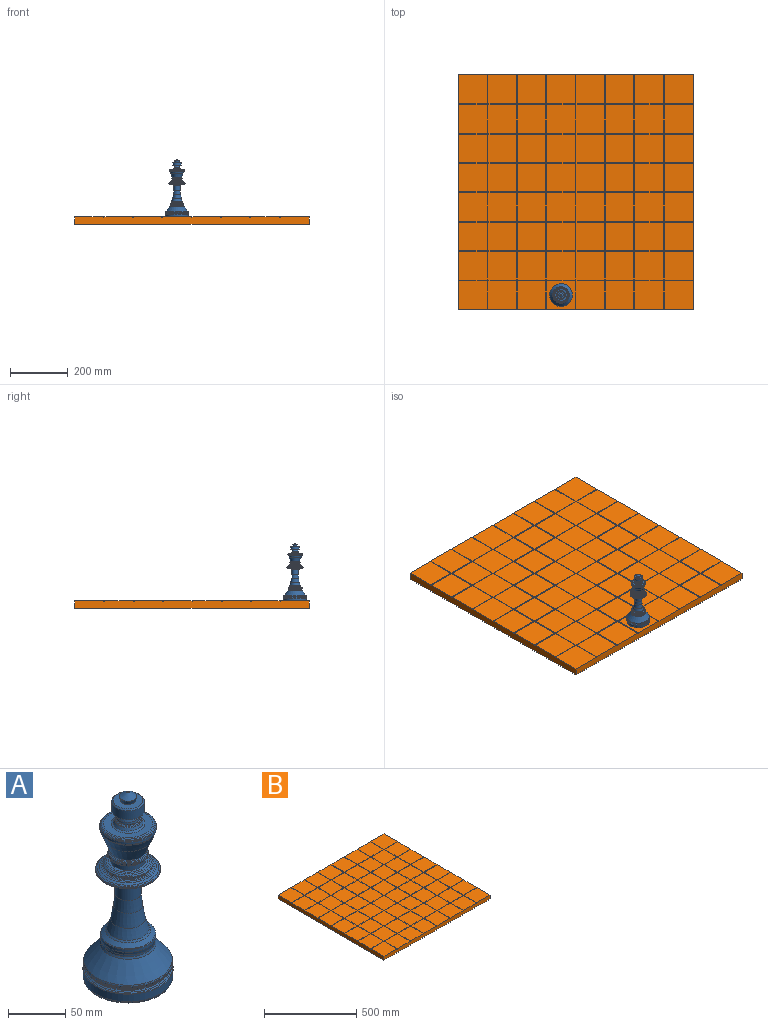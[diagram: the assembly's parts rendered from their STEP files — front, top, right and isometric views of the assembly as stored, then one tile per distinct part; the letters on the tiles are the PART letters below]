
ASSEMBLY  parts=2 mates=1
PART A: 79 faces, bbox 78.8x78.8x198.1 mm
  f0: cone r=0.97mm half-angle=57.7deg, axis (0,0,-1), area 220.6mm2, adj f1,f76
  f1: plane 1.95x1.95mm, normal (0,0,1), area 3mm2, adj f0
  f2: plane 77.2x77.2mm, normal (0,0,-1), area 4681mm2, adj f3
  f3: cone r=39.06mm half-angle=15.9deg, axis (0,0,1), area 409.4mm2, adj f2,f4
  f4: cone r=39.41mm half-angle=2.4deg, axis (0,0,1), area 2062.8mm2, adj f3,f5
  f5: cone r=39.06mm half-angle=38.7deg, axis (0,0,-1), area 138.9mm2, adj f4,f6
  f6: cone r=38mm half-angle=53.7deg, axis (0,0,-1), area 319.8mm2, adj f5,f7
  f7: cone r=36.85mm half-angle=47.9deg, axis (0,0,-1), area 362mm2, adj f6,f8
  f8: cone r=36.53mm half-angle=22.2deg, axis (0,0,-1), area 195.2mm2, adj f7,f9
  f9: cone r=37.16mm half-angle=30.8deg, axis (0,0,1), area 285.3mm2, adj f8,f10
  f10: cone r=38.07mm half-angle=39.3deg, axis (0,0,1), area 338.8mm2, adj f9,f11
  f11: cone r=38.75mm half-angle=27deg, axis (0,0,1), area 362mm2, adj f10,f12
  f12: cone r=39.06mm half-angle=13.8deg, axis (0,0,1), area 315.7mm2, adj f11,f13
  f13: cone r=38.56mm half-angle=22.2deg, axis (0,0,-1), area 322.8mm2, adj f12,f14
  f14: cone r=24.39mm half-angle=38.7deg, axis (0,0,-1), area 4485.2mm2, adj f13,f15
  f15: cone r=23.55mm half-angle=22.2deg, axis (0,0,-1), area 337.6mm2, adj f14,f16
  f16: cylinder r=23.55mm len=47.1mm, axis (0,0,1), area 298.9mm2, adj f15,f17
  f17: cone r=24.1mm half-angle=10.2deg, axis (0,0,1), area 468.6mm2, adj f16,f18
  f18: cylinder r=24.1mm len=48.2mm, axis (0,0,1), area 484.1mm2, adj f17,f19
  f19: cone r=23.65mm half-angle=38.7deg, axis (0,0,-1), area 108.7mm2, adj f18,f20
  f20: cone r=19.7mm half-angle=49.8deg, axis (0,0,-1), area 704.5mm2, adj f19,f21
  f21: cone r=18.38mm half-angle=38.7deg, axis (0,0,-1), area 253mm2, adj f20,f22
  f22: cone r=15.18mm half-angle=17deg, axis (0,0,-1), area 1156.2mm2, adj f21,f23
  f23: cone r=12.68mm half-angle=9.8deg, axis (0,0,-1), area 1278.9mm2, adj f22,f24
  f24: cone r=11.45mm half-angle=5.6deg, axis (0,0,-1), area 967.8mm2, adj f23,f25
  f25: cylinder r=11.45mm len=22.89mm, axis (0,0,1), area 1421.3mm2, adj f24,f26
  f26: plane 23.55x23.55mm, normal (0,0,-1), area 23.9mm2, adj f25,f27
  f27: cone r=13.64mm half-angle=80.8deg, axis (0,0,1), area 150.7mm2, adj f26,f28
  f28: cone r=16.33mm half-angle=82deg, axis (0,0,1), area 256.1mm2, adj f27,f29
  f29: cone r=18.9mm half-angle=80.5deg, axis (0,0,1), area 288.1mm2, adj f28,f30
  f30: cone r=21.09mm half-angle=80.1deg, axis (0,0,1), area 279.2mm2, adj f29,f31
  f31: cone r=27.01mm half-angle=67.8deg, axis (0,0,1), area 965.6mm2, adj f30,f32
  f32: cone r=27.76mm half-angle=51.3deg, axis (0,0,1), area 166.2mm2, adj f31,f33
  f33: cone r=28.46mm half-angle=45.8deg, axis (0,0,1), area 172mm2, adj f32,f34
  f34: cylinder r=28.46mm len=56.92mm, axis (0,0,1), area 138.1mm2, adj f33,f35
  f35: cone r=28.09mm half-angle=22.2deg, axis (0,0,-1), area 174.9mm2, adj f34,f36
  f36: cone r=26.85mm half-angle=58.5deg, axis (0,0,-1), area 249.3mm2, adj f35,f37
  f37: cone r=24.76mm half-angle=62.2deg, axis (0,0,-1), area 384.1mm2, adj f36,f38
  f38: cone r=23.21mm half-angle=66.4deg, axis (0,0,-1), area 255.1mm2, adj f37,f39
  f39: cone r=22.05mm half-angle=68.6deg, axis (0,0,-1), area 176.6mm2, adj f38,f40
  f40: cone r=21.2mm half-angle=60.8deg, axis (0,0,-1), area 133.1mm2, adj f39,f41
  f41: cylinder r=21.2mm len=42.4mm, axis (0,0,1), area 97.1mm2, adj f40,f42
  f42: cone r=21.58mm half-angle=26.6deg, axis (0,0,1), area 113.3mm2, adj f41,f43
  f43: cylinder r=21.58mm len=43.15mm, axis (0,0,1), area 109.1mm2, adj f42,f44
  f44: cone r=20.32mm half-angle=50.6deg, axis (0,0,-1), area 214mm2, adj f43,f45
  f45: cone r=18.89mm half-angle=61.5deg, axis (0,0,-1), area 200.9mm2, adj f44,f46
  f46: cone r=17.3mm half-angle=76.6deg, axis (0,0,-1), area 185.1mm2, adj f45,f47
  f47: cone r=15.18mm half-angle=82.6deg, axis (0,0,-1), area 218.4mm2, adj f46,f48
  f48: cylinder r=15.18mm len=30.36mm, axis (0,0,1), area 483.2mm2, adj f47,f49
  f49: cone r=16.19mm half-angle=67.8deg, axis (0,0,1), area 108.2mm2, adj f48,f50
  f50: cone r=16.72mm half-angle=46.4deg, axis (0,0,1), area 75.4mm2, adj f49,f51
  f51: cone r=17.18mm half-angle=35.8deg, axis (0,0,1), area 82.5mm2, adj f50,f52
  f52: cone r=17.7mm half-angle=18.7deg, axis (0,0,1), area 180.3mm2, adj f51,f53
  f53: cone r=17.53mm half-angle=10.4deg, axis (0,0,-1), area 107.5mm2, adj f52,f54
  f54: cone r=16.97mm half-angle=35.4deg, axis (0,0,-1), area 103.6mm2, adj f53,f55
  f55: cone r=16.07mm half-angle=57.4deg, axis (0,0,-1), area 111.5mm2, adj f54,f56
  f56: cone r=15.39mm half-angle=45deg, axis (0,0,-1), area 94.9mm2, adj f55,f57
  f57: cone r=20.82mm half-angle=22.5deg, axis (0,0,1), area 1615.7mm2, adj f56,f58
  f58: cone r=24.44mm half-angle=21.4deg, axis (0,0,1), area 1412.7mm2, adj f57,f59
  f59: cone r=24.76mm half-angle=18deg, axis (0,0,1), area 159.4mm2, adj f58,f60
  f60: cylinder r=24.76mm len=49.52mm, axis (0,0,1), area 398.5mm2, adj f59,f61
  f61: cone r=24.44mm half-angle=22.2deg, axis (0,0,-1), area 130.6mm2, adj f60,f62
  f62: cone r=23.99mm half-angle=39.3deg, axis (0,0,-1), area 108.7mm2, adj f61,f63
  f63: cone r=23.06mm half-angle=53.9deg, axis (0,0,-1), area 170.2mm2, adj f62,f64
  f64: cone r=21.5mm half-angle=75.5deg, axis (0,0,-1), area 225.4mm2, adj f63,f65
  f65: plane 43x43mm, normal (0,0,1), area 765.2mm2, adj f64,f66
  f66: cone r=12.88mm half-angle=62.8deg, axis (0,0,-1), area 186.6mm2, adj f65,f67
  f67: cone r=11.57mm half-angle=27deg, axis (0,0,-1), area 221.1mm2, adj f66,f68
  f68: cone r=10.56mm half-angle=73.3deg, axis (0,0,-1), area 73mm2, adj f67,f69
  f69: cone r=9.48mm half-angle=47.8deg, axis (0,0,-1), area 91.9mm2, adj f68,f70
  f70: cone r=10.19mm half-angle=27deg, axis (0,0,1), area 95.9mm2, adj f69,f71
  f71: cone r=9.85mm half-angle=9.7deg, axis (0,0,-1), area 125.7mm2, adj f70,f72
  f72: cone r=7.91mm half-angle=22.2deg, axis (0,0,-1), area 287.1mm2, adj f71,f73
  f73: plane 26.01x26.01mm, normal (0,0,-1), area 334.8mm2, adj f72,f78
  f74: cylinder r=14.27mm len=28.55mm, axis (0,0,1), area 846.6mm2, adj f77,f78
  f75: plane 26.01x26.01mm, normal (0,0,1), area 395mm2, adj f76,f77
  f76: cone r=7.77mm half-angle=15.4deg, axis (0,0,1), area 200.7mm2, adj f0,f75
  f77: cone r=13mm half-angle=45deg, axis (0,0,-1), area 153.9mm2, adj f74,f75
  f78: cone r=14.27mm half-angle=45deg, axis (0,0,1), area 153.9mm2, adj f73,f74
PART B: 294 faces, bbox 812.8x812.8x25.4 mm
  f0: plane 812.8x25.4mm, normal (0,-1,0), area 20600mm2, adj f1,f2,f3,f4,f5,f6,f7,f8
  f1: plane 812.8x25.4mm, normal (-1,0,0), area 20600mm2, adj f0,f9,f22,f24,f25,f26,f27,f28
  f2: plane 99.06x99.06mm, normal (0,0,1), area 9812.9mm2, adj f0,f35,f36,f37
  f3: plane 99.06x99.06mm, normal (0,0,1), area 9812.9mm2, adj f0,f38,f39,f40
  f4: plane 99.06x99.06mm, normal (0,0,1), area 9812.9mm2, adj f0,f41,f42,f43
  f5: plane 99.06x99.06mm, normal (0,0,1), area 9812.9mm2, adj f0,f44,f45,f46
  f6: plane 99.06x99.06mm, normal (0,0,1), area 9812.9mm2, adj f0,f47,f48,f49
  f7: plane 99.06x99.06mm, normal (0,0,1), area 9812.9mm2, adj f0,f50,f51,f52
  f8: plane 101.6x99.06mm, normal (0,0,1), area 10064.5mm2, adj f0,f29,f53,f54
  f9: plane 99.06x99.06mm, normal (0,0,1), area 9812.9mm2, adj f0,f1,f33,f34
  f10: plane 101.6x99.06mm, normal (0,0,1), area 10064.5mm2, adj f29,f55,f56,f57
  f11: plane 101.6x99.06mm, normal (0,0,1), area 10064.5mm2, adj f29,f58,f59,f60
  f12: plane 101.6x99.06mm, normal (0,0,1), area 10064.5mm2, adj f29,f61,f62,f63
  f13: plane 101.6x99.06mm, normal (0,0,1), area 10064.5mm2, adj f29,f64,f65,f66
  f14: plane 101.6x99.06mm, normal (0,0,1), area 10064.5mm2, adj f29,f67,f68,f69
  f15: plane 101.6x99.06mm, normal (0,0,1), area 10064.5mm2, adj f29,f70,f71,f72
  f16: plane 101.6x99.06mm, normal (0,0,1), area 10064.5mm2, adj f30,f75,f76,f77
  f17: plane 101.6x99.06mm, normal (0,0,1), area 10064.5mm2, adj f30,f78,f79,f80
  f18: plane 101.6x99.06mm, normal (0,0,1), area 10064.5mm2, adj f30,f81,f82,f83
  f19: plane 101.6x99.06mm, normal (0,0,1), area 10064.5mm2, adj f30,f84,f85,f86
  f20: plane 101.6x99.06mm, normal (0,0,1), area 10064.5mm2, adj f30,f87,f88,f89
  f21: plane 101.6x99.06mm, normal (0,0,1), area 10064.5mm2, adj f30,f90,f91,f92
  f22: plane 101.6x99.06mm, normal (0,0,1), area 10064.5mm2, adj f1,f30,f93,f94
  f23: plane 101.6x101.6mm, normal (0,0,1), area 10322.6mm2, adj f29,f30,f73,f74
  f24: plane 99.06x99.06mm, normal (0,0,1), area 9812.9mm2, adj f1,f95,f96,f97
  f25: plane 99.06x99.06mm, normal (0,0,1), area 9812.9mm2, adj f1,f98,f99,f100
  f26: plane 99.06x99.06mm, normal (0,0,1), area 9812.9mm2, adj f1,f101,f102,f103
  f27: plane 99.06x99.06mm, normal (0,0,1), area 9812.9mm2, adj f1,f104,f105,f106
  f28: plane 99.06x99.06mm, normal (0,0,1), area 9812.9mm2, adj f1,f107,f108,f109
  f29: plane 812.8x25.4mm, normal (1,0,0), area 20600mm2, adj f0,f8,f10,f11,f12,f13,f14,f15
  f30: plane 812.8x25.4mm, normal (0,1,0), area 20600mm2, adj f1,f16,f17,f18,f19,f20,f21,f22
  f31: plane 99.06x99.06mm, normal (0,0,1), area 9812.9mm2, adj f1,f110,f111,f256
  f32: plane 812.8x812.8mm, normal (0,0,-1), area 660643.8mm2, adj f0,f1,f29,f30
  f33: plane 99.06x2.54mm, normal (0,1,0), area 251.6mm2, adj f1,f9,f34,f257
  f34: plane 99.06x2.54mm, normal (1,0,0), area 251.6mm2, adj f0,f9,f33,f257
  f35: plane 99.06x2.54mm, normal (-1,0,0), area 251.6mm2, adj f0,f2,f36,f257
  f36: plane 99.06x2.54mm, normal (0,1,0), area 251.6mm2, adj f2,f35,f37,f257
  f37: plane 99.06x2.54mm, normal (1,0,0), area 251.6mm2, adj f0,f2,f36,f257
  f38: plane 99.06x2.54mm, normal (-1,0,0), area 251.6mm2, adj f0,f3,f39,f257
  f39: plane 99.06x2.54mm, normal (0,1,0), area 251.6mm2, adj f3,f38,f40,f257
  f40: plane 99.06x2.54mm, normal (1,0,0), area 251.6mm2, adj f0,f3,f39,f257
  f41: plane 99.06x2.54mm, normal (-1,0,0), area 251.6mm2, adj f0,f4,f42,f257
  f42: plane 99.06x2.54mm, normal (0,1,0), area 251.6mm2, adj f4,f41,f43,f257
  f43: plane 99.06x2.54mm, normal (1,0,0), area 251.6mm2, adj f0,f4,f42,f257
  f44: plane 99.06x2.54mm, normal (-1,0,0), area 251.6mm2, adj f0,f5,f45,f257
  f45: plane 99.06x2.54mm, normal (0,1,0), area 251.6mm2, adj f5,f44,f46,f257
  f46: plane 99.06x2.54mm, normal (1,0,0), area 251.6mm2, adj f0,f5,f45,f257
  f47: plane 99.06x2.54mm, normal (-1,0,0), area 251.6mm2, adj f0,f6,f48,f257
  f48: plane 99.06x2.54mm, normal (0,1,0), area 251.6mm2, adj f6,f47,f49,f257
  f49: plane 99.06x2.54mm, normal (1,0,0), area 251.6mm2, adj f0,f6,f48,f257
  f50: plane 99.06x2.54mm, normal (-1,0,0), area 251.6mm2, adj f0,f7,f51,f257
  f51: plane 99.06x2.54mm, normal (0,1,0), area 251.6mm2, adj f7,f50,f52,f257
  f52: plane 99.06x2.54mm, normal (1,0,0), area 251.6mm2, adj f0,f7,f51,f257
  f53: plane 99.06x2.54mm, normal (-1,0,0), area 251.6mm2, adj f0,f8,f54,f257
  f54: plane 101.6x2.54mm, normal (0,1,0), area 258.1mm2, adj f8,f29,f53,f257
  f55: plane 101.6x2.54mm, normal (0,-1,0), area 258.1mm2, adj f10,f29,f56,f257
  f56: plane 99.06x2.54mm, normal (-1,0,0), area 251.6mm2, adj f10,f55,f57,f257
  f57: plane 101.6x2.54mm, normal (0,1,0), area 258.1mm2, adj f10,f29,f56,f257
  f58: plane 101.6x2.54mm, normal (0,-1,0), area 258.1mm2, adj f11,f29,f59,f257
  f59: plane 99.06x2.54mm, normal (-1,0,0), area 251.6mm2, adj f11,f58,f60,f257
  f60: plane 101.6x2.54mm, normal (0,1,0), area 258.1mm2, adj f11,f29,f59,f257
  f61: plane 101.6x2.54mm, normal (0,-1,0), area 258.1mm2, adj f12,f29,f62,f257
  f62: plane 99.06x2.54mm, normal (-1,0,0), area 251.6mm2, adj f12,f61,f63,f257
  f63: plane 101.6x2.54mm, normal (0,1,0), area 258.1mm2, adj f12,f29,f62,f257
  f64: plane 101.6x2.54mm, normal (0,-1,0), area 258.1mm2, adj f13,f29,f65,f257
  f65: plane 99.06x2.54mm, normal (-1,0,0), area 251.6mm2, adj f13,f64,f66,f257
  f66: plane 101.6x2.54mm, normal (0,1,0), area 258.1mm2, adj f13,f29,f65,f257
  f67: plane 101.6x2.54mm, normal (0,-1,0), area 258.1mm2, adj f14,f29,f68,f257
  f68: plane 99.06x2.54mm, normal (-1,0,0), area 251.6mm2, adj f14,f67,f69,f257
  f69: plane 101.6x2.54mm, normal (0,1,0), area 258.1mm2, adj f14,f29,f68,f257
  f70: plane 101.6x2.54mm, normal (0,-1,0), area 258.1mm2, adj f15,f29,f71,f257
  f71: plane 99.06x2.54mm, normal (-1,0,0), area 251.6mm2, adj f15,f70,f72,f257
  f72: plane 101.6x2.54mm, normal (0,1,0), area 258.1mm2, adj f15,f29,f71,f257
  f73: plane 101.6x2.54mm, normal (0,-1,0), area 258.1mm2, adj f23,f29,f74,f257
  f74: plane 101.6x2.54mm, normal (-1,0,0), area 258.1mm2, adj f23,f30,f73,f257
  f75: plane 101.6x2.54mm, normal (1,0,0), area 258.1mm2, adj f16,f30,f76,f257
  f76: plane 99.06x2.54mm, normal (0,-1,0), area 251.6mm2, adj f16,f75,f77,f257
  f77: plane 101.6x2.54mm, normal (-1,0,0), area 258.1mm2, adj f16,f30,f76,f257
  f78: plane 101.6x2.54mm, normal (1,0,0), area 258.1mm2, adj f17,f30,f79,f257
  f79: plane 99.06x2.54mm, normal (0,-1,0), area 251.6mm2, adj f17,f78,f80,f257
  f80: plane 101.6x2.54mm, normal (-1,0,0), area 258.1mm2, adj f17,f30,f79,f257
  f81: plane 101.6x2.54mm, normal (1,0,0), area 258.1mm2, adj f18,f30,f82,f257
  f82: plane 99.06x2.54mm, normal (0,-1,0), area 251.6mm2, adj f18,f81,f83,f257
  f83: plane 101.6x2.54mm, normal (-1,0,0), area 258.1mm2, adj f18,f30,f82,f257
  f84: plane 101.6x2.54mm, normal (1,0,0), area 258.1mm2, adj f19,f30,f85,f257
  f85: plane 99.06x2.54mm, normal (0,-1,0), area 251.6mm2, adj f19,f84,f86,f257
  f86: plane 101.6x2.54mm, normal (-1,0,0), area 258.1mm2, adj f19,f30,f85,f257
  f87: plane 101.6x2.54mm, normal (1,0,0), area 258.1mm2, adj f20,f30,f88,f257
  f88: plane 99.06x2.54mm, normal (0,-1,0), area 251.6mm2, adj f20,f87,f89,f257
  f89: plane 101.6x2.54mm, normal (-1,0,0), area 258.1mm2, adj f20,f30,f88,f257
  f90: plane 101.6x2.54mm, normal (1,0,0), area 258.1mm2, adj f21,f30,f91,f257
  f91: plane 99.06x2.54mm, normal (0,-1,0), area 251.6mm2, adj f21,f90,f92,f257
  f92: plane 101.6x2.54mm, normal (-1,0,0), area 258.1mm2, adj f21,f30,f91,f257
  f93: plane 101.6x2.54mm, normal (1,0,0), area 258.1mm2, adj f22,f30,f94,f257
  f94: plane 99.06x2.54mm, normal (0,-1,0), area 251.6mm2, adj f1,f22,f93,f257
  f95: plane 99.06x2.54mm, normal (0,1,0), area 251.6mm2, adj f1,f24,f96,f257
  f96: plane 99.06x2.54mm, normal (1,0,0), area 251.6mm2, adj f24,f95,f97,f257
  f97: plane 99.06x2.54mm, normal (0,-1,0), area 251.6mm2, adj f1,f24,f96,f257
  f98: plane 99.06x2.54mm, normal (0,1,0), area 251.6mm2, adj f1,f25,f99,f257
  f99: plane 99.06x2.54mm, normal (1,0,0), area 251.6mm2, adj f25,f98,f100,f257
  f100: plane 99.06x2.54mm, normal (0,-1,0), area 251.6mm2, adj f1,f25,f99,f257
  f101: plane 99.06x2.54mm, normal (0,1,0), area 251.6mm2, adj f1,f26,f102,f257
  f102: plane 99.06x2.54mm, normal (1,0,0), area 251.6mm2, adj f26,f101,f103,f257
  f103: plane 99.06x2.54mm, normal (0,-1,0), area 251.6mm2, adj f1,f26,f102,f257
  f104: plane 99.06x2.54mm, normal (0,1,0), area 251.6mm2, adj f1,f27,f105,f257
  f105: plane 99.06x2.54mm, normal (1,0,0), area 251.6mm2, adj f27,f104,f106,f257
  f106: plane 99.06x2.54mm, normal (0,-1,0), area 251.6mm2, adj f1,f27,f105,f257
  f107: plane 99.06x2.54mm, normal (0,1,0), area 251.6mm2, adj f1,f28,f108,f257
  f108: plane 99.06x2.54mm, normal (1,0,0), area 251.6mm2, adj f28,f107,f109,f257
  f109: plane 99.06x2.54mm, normal (0,-1,0), area 251.6mm2, adj f1,f28,f108,f257
  f110: plane 99.06x2.54mm, normal (0,1,0), area 251.6mm2, adj f1,f31,f111,f257
  f111: plane 99.06x2.54mm, normal (1,0,0), area 251.6mm2, adj f31,f110,f256,f257
  f112: plane 99.06x2.54mm, normal (-1,0,0), area 251.6mm2, adj f113,f220,f257,f293
  f113: plane 99.06x2.54mm, normal (0,1,0), area 251.6mm2, adj f112,f114,f257,f293
  f114: plane 99.06x2.54mm, normal (1,0,0), area 251.6mm2, adj f113,f220,f257,f293
  f115: plane 99.06x2.54mm, normal (-1,0,0), area 251.6mm2, adj f116,f221,f257,f292
  f116: plane 99.06x2.54mm, normal (0,1,0), area 251.6mm2, adj f115,f117,f257,f292
  f117: plane 99.06x2.54mm, normal (1,0,0), area 251.6mm2, adj f116,f221,f257,f292
  f118: plane 99.06x2.54mm, normal (-1,0,0), area 251.6mm2, adj f119,f222,f257,f291
  f119: plane 99.06x2.54mm, normal (0,1,0), area 251.6mm2, adj f118,f120,f257,f291
  f120: plane 99.06x2.54mm, normal (1,0,0), area 251.6mm2, adj f119,f222,f257,f291
  f121: plane 99.06x2.54mm, normal (-1,0,0), area 251.6mm2, adj f122,f223,f257,f290
  f122: plane 99.06x2.54mm, normal (0,1,0), area 251.6mm2, adj f121,f123,f257,f290
  f123: plane 99.06x2.54mm, normal (1,0,0), area 251.6mm2, adj f122,f223,f257,f290
  f124: plane 99.06x2.54mm, normal (-1,0,0), area 251.6mm2, adj f125,f224,f257,f289
  f125: plane 99.06x2.54mm, normal (0,1,0), area 251.6mm2, adj f124,f126,f257,f289
  f126: plane 99.06x2.54mm, normal (1,0,0), area 251.6mm2, adj f125,f224,f257,f289
  f127: plane 99.06x2.54mm, normal (-1,0,0), area 251.6mm2, adj f128,f225,f257,f288
  f128: plane 99.06x2.54mm, normal (0,1,0), area 251.6mm2, adj f127,f129,f257,f288
  f129: plane 99.06x2.54mm, normal (1,0,0), area 251.6mm2, adj f128,f225,f257,f288
  f130: plane 99.06x2.54mm, normal (-1,0,0), area 251.6mm2, adj f131,f226,f257,f287
  f131: plane 99.06x2.54mm, normal (0,1,0), area 251.6mm2, adj f130,f132,f257,f287
  f132: plane 99.06x2.54mm, normal (1,0,0), area 251.6mm2, adj f131,f226,f257,f287
  f133: plane 99.06x2.54mm, normal (-1,0,0), area 251.6mm2, adj f134,f227,f257,f286
  f134: plane 99.06x2.54mm, normal (0,1,0), area 251.6mm2, adj f133,f135,f257,f286
  f135: plane 99.06x2.54mm, normal (1,0,0), area 251.6mm2, adj f134,f227,f257,f286
  f136: plane 99.06x2.54mm, normal (-1,0,0), area 251.6mm2, adj f137,f228,f257,f285
  f137: plane 99.06x2.54mm, normal (0,1,0), area 251.6mm2, adj f136,f138,f257,f285
  f138: plane 99.06x2.54mm, normal (1,0,0), area 251.6mm2, adj f137,f228,f257,f285
  f139: plane 99.06x2.54mm, normal (-1,0,0), area 251.6mm2, adj f140,f229,f257,f284
  f140: plane 99.06x2.54mm, normal (0,1,0), area 251.6mm2, adj f139,f141,f257,f284
  f141: plane 99.06x2.54mm, normal (1,0,0), area 251.6mm2, adj f140,f229,f257,f284
  f142: plane 99.06x2.54mm, normal (-1,0,0), area 251.6mm2, adj f143,f230,f257,f283
  f143: plane 99.06x2.54mm, normal (0,1,0), area 251.6mm2, adj f142,f144,f257,f283
  f144: plane 99.06x2.54mm, normal (1,0,0), area 251.6mm2, adj f143,f230,f257,f283
  f145: plane 99.06x2.54mm, normal (-1,0,0), area 251.6mm2, adj f146,f231,f257,f282
  f146: plane 99.06x2.54mm, normal (0,1,0), area 251.6mm2, adj f145,f147,f257,f282
  f147: plane 99.06x2.54mm, normal (1,0,0), area 251.6mm2, adj f146,f231,f257,f282
  f148: plane 99.06x2.54mm, normal (-1,0,0), area 251.6mm2, adj f149,f232,f257,f281
  f149: plane 99.06x2.54mm, normal (0,1,0), area 251.6mm2, adj f148,f150,f257,f281
  f150: plane 99.06x2.54mm, normal (1,0,0), area 251.6mm2, adj f149,f232,f257,f281
  f151: plane 99.06x2.54mm, normal (-1,0,0), area 251.6mm2, adj f152,f233,f257,f280
  f152: plane 99.06x2.54mm, normal (0,1,0), area 251.6mm2, adj f151,f153,f257,f280
  f153: plane 99.06x2.54mm, normal (1,0,0), area 251.6mm2, adj f152,f233,f257,f280
  f154: plane 99.06x2.54mm, normal (-1,0,0), area 251.6mm2, adj f155,f234,f257,f279
  f155: plane 99.06x2.54mm, normal (0,1,0), area 251.6mm2, adj f154,f156,f257,f279
  f156: plane 99.06x2.54mm, normal (1,0,0), area 251.6mm2, adj f155,f234,f257,f279
  f157: plane 99.06x2.54mm, normal (-1,0,0), area 251.6mm2, adj f158,f235,f257,f278
  f158: plane 99.06x2.54mm, normal (0,1,0), area 251.6mm2, adj f157,f159,f257,f278
  f159: plane 99.06x2.54mm, normal (1,0,0), area 251.6mm2, adj f158,f235,f257,f278
  f160: plane 99.06x2.54mm, normal (-1,0,0), area 251.6mm2, adj f161,f236,f257,f277
  f161: plane 99.06x2.54mm, normal (0,1,0), area 251.6mm2, adj f160,f162,f257,f277
  f162: plane 99.06x2.54mm, normal (1,0,0), area 251.6mm2, adj f161,f236,f257,f277
  f163: plane 99.06x2.54mm, normal (-1,0,0), area 251.6mm2, adj f164,f237,f257,f276
  f164: plane 99.06x2.54mm, normal (0,1,0), area 251.6mm2, adj f163,f165,f257,f276
  f165: plane 99.06x2.54mm, normal (1,0,0), area 251.6mm2, adj f164,f237,f257,f276
  f166: plane 99.06x2.54mm, normal (-1,0,0), area 251.6mm2, adj f167,f238,f257,f275
  f167: plane 99.06x2.54mm, normal (0,1,0), area 251.6mm2, adj f166,f168,f257,f275
  f168: plane 99.06x2.54mm, normal (1,0,0), area 251.6mm2, adj f167,f238,f257,f275
  f169: plane 99.06x2.54mm, normal (-1,0,0), area 251.6mm2, adj f170,f239,f257,f274
  f170: plane 99.06x2.54mm, normal (0,1,0), area 251.6mm2, adj f169,f171,f257,f274
  f171: plane 99.06x2.54mm, normal (1,0,0), area 251.6mm2, adj f170,f239,f257,f274
  f172: plane 99.06x2.54mm, normal (-1,0,0), area 251.6mm2, adj f173,f240,f257,f273
  f173: plane 99.06x2.54mm, normal (0,1,0), area 251.6mm2, adj f172,f174,f257,f273
  f174: plane 99.06x2.54mm, normal (1,0,0), area 251.6mm2, adj f173,f240,f257,f273
  f175: plane 99.06x2.54mm, normal (-1,0,0), area 251.6mm2, adj f176,f241,f257,f272
  f176: plane 99.06x2.54mm, normal (0,1,0), area 251.6mm2, adj f175,f177,f257,f272
  f177: plane 99.06x2.54mm, normal (1,0,0), area 251.6mm2, adj f176,f241,f257,f272
  f178: plane 99.06x2.54mm, normal (-1,0,0), area 251.6mm2, adj f179,f242,f257,f271
  f179: plane 99.06x2.54mm, normal (0,1,0), area 251.6mm2, adj f178,f180,f257,f271
  f180: plane 99.06x2.54mm, normal (1,0,0), area 251.6mm2, adj f179,f242,f257,f271
  f181: plane 99.06x2.54mm, normal (-1,0,0), area 251.6mm2, adj f182,f243,f257,f270
  f182: plane 99.06x2.54mm, normal (0,1,0), area 251.6mm2, adj f181,f183,f257,f270
  f183: plane 99.06x2.54mm, normal (1,0,0), area 251.6mm2, adj f182,f243,f257,f270
  f184: plane 99.06x2.54mm, normal (-1,0,0), area 251.6mm2, adj f185,f244,f257,f269
  f185: plane 99.06x2.54mm, normal (0,1,0), area 251.6mm2, adj f184,f186,f257,f269
  f186: plane 99.06x2.54mm, normal (1,0,0), area 251.6mm2, adj f185,f244,f257,f269
  f187: plane 99.06x2.54mm, normal (-1,0,0), area 251.6mm2, adj f188,f245,f257,f268
  f188: plane 99.06x2.54mm, normal (0,1,0), area 251.6mm2, adj f187,f189,f257,f268
  f189: plane 99.06x2.54mm, normal (1,0,0), area 251.6mm2, adj f188,f245,f257,f268
  f190: plane 99.06x2.54mm, normal (-1,0,0), area 251.6mm2, adj f191,f246,f257,f267
  f191: plane 99.06x2.54mm, normal (0,1,0), area 251.6mm2, adj f190,f192,f257,f267
  f192: plane 99.06x2.54mm, normal (1,0,0), area 251.6mm2, adj f191,f246,f257,f267
  f193: plane 99.06x2.54mm, normal (-1,0,0), area 251.6mm2, adj f194,f247,f257,f266
  f194: plane 99.06x2.54mm, normal (0,1,0), area 251.6mm2, adj f193,f195,f257,f266
  f195: plane 99.06x2.54mm, normal (1,0,0), area 251.6mm2, adj f194,f247,f257,f266
  f196: plane 99.06x2.54mm, normal (-1,0,0), area 251.6mm2, adj f197,f248,f257,f265
  f197: plane 99.06x2.54mm, normal (0,1,0), area 251.6mm2, adj f196,f198,f257,f265
  f198: plane 99.06x2.54mm, normal (1,0,0), area 251.6mm2, adj f197,f248,f257,f265
  f199: plane 99.06x2.54mm, normal (-1,0,0), area 251.6mm2, adj f200,f249,f257,f264
  f200: plane 99.06x2.54mm, normal (0,1,0), area 251.6mm2, adj f199,f201,f257,f264
  f201: plane 99.06x2.54mm, normal (1,0,0), area 251.6mm2, adj f200,f249,f257,f264
  f202: plane 99.06x2.54mm, normal (0,-1,0), area 251.6mm2, adj f203,f250,f257,f263
  f203: plane 99.06x2.54mm, normal (-1,0,0), area 251.6mm2, adj f202,f204,f257,f263
  f204: plane 99.06x2.54mm, normal (0,1,0), area 251.6mm2, adj f203,f250,f257,f263
  f205: plane 99.06x2.54mm, normal (0,-1,0), area 251.6mm2, adj f206,f251,f257,f262
  f206: plane 99.06x2.54mm, normal (-1,0,0), area 251.6mm2, adj f205,f207,f257,f262
  f207: plane 99.06x2.54mm, normal (0,1,0), area 251.6mm2, adj f206,f251,f257,f262
  f208: plane 99.06x2.54mm, normal (0,-1,0), area 251.6mm2, adj f209,f252,f257,f261
  f209: plane 99.06x2.54mm, normal (-1,0,0), area 251.6mm2, adj f208,f210,f257,f261
  f210: plane 99.06x2.54mm, normal (0,1,0), area 251.6mm2, adj f209,f252,f257,f261
  f211: plane 99.06x2.54mm, normal (0,-1,0), area 251.6mm2, adj f212,f253,f257,f260
  f212: plane 99.06x2.54mm, normal (-1,0,0), area 251.6mm2, adj f211,f213,f257,f260
  f213: plane 99.06x2.54mm, normal (0,1,0), area 251.6mm2, adj f212,f253,f257,f260
  f214: plane 99.06x2.54mm, normal (0,-1,0), area 251.6mm2, adj f215,f254,f257,f259
  f215: plane 99.06x2.54mm, normal (-1,0,0), area 251.6mm2, adj f214,f216,f257,f259
  f216: plane 99.06x2.54mm, normal (0,1,0), area 251.6mm2, adj f215,f254,f257,f259
  f217: plane 99.06x2.54mm, normal (0,-1,0), area 251.6mm2, adj f218,f255,f257,f258
  f218: plane 99.06x2.54mm, normal (-1,0,0), area 251.6mm2, adj f217,f219,f257,f258
  f219: plane 99.06x2.54mm, normal (0,1,0), area 251.6mm2, adj f218,f255,f257,f258
  f220: plane 99.06x2.54mm, normal (0,-1,0), area 251.6mm2, adj f112,f114,f257,f293
  f221: plane 99.06x2.54mm, normal (0,-1,0), area 251.6mm2, adj f115,f117,f257,f292
  f222: plane 99.06x2.54mm, normal (0,-1,0), area 251.6mm2, adj f118,f120,f257,f291
  f223: plane 99.06x2.54mm, normal (0,-1,0), area 251.6mm2, adj f121,f123,f257,f290
  f224: plane 99.06x2.54mm, normal (0,-1,0), area 251.6mm2, adj f124,f126,f257,f289
  f225: plane 99.06x2.54mm, normal (0,-1,0), area 251.6mm2, adj f127,f129,f257,f288
  f226: plane 99.06x2.54mm, normal (0,-1,0), area 251.6mm2, adj f130,f132,f257,f287
  f227: plane 99.06x2.54mm, normal (0,-1,0), area 251.6mm2, adj f133,f135,f257,f286
  f228: plane 99.06x2.54mm, normal (0,-1,0), area 251.6mm2, adj f136,f138,f257,f285
  f229: plane 99.06x2.54mm, normal (0,-1,0), area 251.6mm2, adj f139,f141,f257,f284
  f230: plane 99.06x2.54mm, normal (0,-1,0), area 251.6mm2, adj f142,f144,f257,f283
  f231: plane 99.06x2.54mm, normal (0,-1,0), area 251.6mm2, adj f145,f147,f257,f282
  f232: plane 99.06x2.54mm, normal (0,-1,0), area 251.6mm2, adj f148,f150,f257,f281
  f233: plane 99.06x2.54mm, normal (0,-1,0), area 251.6mm2, adj f151,f153,f257,f280
  f234: plane 99.06x2.54mm, normal (0,-1,0), area 251.6mm2, adj f154,f156,f257,f279
  f235: plane 99.06x2.54mm, normal (0,-1,0), area 251.6mm2, adj f157,f159,f257,f278
  f236: plane 99.06x2.54mm, normal (0,-1,0), area 251.6mm2, adj f160,f162,f257,f277
  f237: plane 99.06x2.54mm, normal (0,-1,0), area 251.6mm2, adj f163,f165,f257,f276
  f238: plane 99.06x2.54mm, normal (0,-1,0), area 251.6mm2, adj f166,f168,f257,f275
  f239: plane 99.06x2.54mm, normal (0,-1,0), area 251.6mm2, adj f169,f171,f257,f274
  f240: plane 99.06x2.54mm, normal (0,-1,0), area 251.6mm2, adj f172,f174,f257,f273
  f241: plane 99.06x2.54mm, normal (0,-1,0), area 251.6mm2, adj f175,f177,f257,f272
  f242: plane 99.06x2.54mm, normal (0,-1,0), area 251.6mm2, adj f178,f180,f257,f271
  f243: plane 99.06x2.54mm, normal (0,-1,0), area 251.6mm2, adj f181,f183,f257,f270
  f244: plane 99.06x2.54mm, normal (0,-1,0), area 251.6mm2, adj f184,f186,f257,f269
  f245: plane 99.06x2.54mm, normal (0,-1,0), area 251.6mm2, adj f187,f189,f257,f268
  f246: plane 99.06x2.54mm, normal (0,-1,0), area 251.6mm2, adj f190,f192,f257,f267
  f247: plane 99.06x2.54mm, normal (0,-1,0), area 251.6mm2, adj f193,f195,f257,f266
  f248: plane 99.06x2.54mm, normal (0,-1,0), area 251.6mm2, adj f196,f198,f257,f265
  f249: plane 99.06x2.54mm, normal (0,-1,0), area 251.6mm2, adj f199,f201,f257,f264
  f250: plane 99.06x2.54mm, normal (1,0,0), area 251.6mm2, adj f202,f204,f257,f263
  f251: plane 99.06x2.54mm, normal (1,0,0), area 251.6mm2, adj f205,f207,f257,f262
  f252: plane 99.06x2.54mm, normal (1,0,0), area 251.6mm2, adj f208,f210,f257,f261
  f253: plane 99.06x2.54mm, normal (1,0,0), area 251.6mm2, adj f211,f213,f257,f260
  f254: plane 99.06x2.54mm, normal (1,0,0), area 251.6mm2, adj f214,f216,f257,f259
  f255: plane 99.06x2.54mm, normal (1,0,0), area 251.6mm2, adj f217,f219,f257,f258
  f256: plane 99.06x2.54mm, normal (0,-1,0), area 251.6mm2, adj f1,f31,f111,f257
  f257: plane 812.8x812.8mm, normal (0,0,1), area 28587mm2, adj f0,f1,f29,f30,f33,f34,f35,f36
  f258: plane 99.06x99.06mm, normal (0,0,1), area 9812.9mm2, adj f217,f218,f219,f255
  f259: plane 99.06x99.06mm, normal (0,0,1), area 9812.9mm2, adj f214,f215,f216,f254
  f260: plane 99.06x99.06mm, normal (0,0,1), area 9812.9mm2, adj f211,f212,f213,f253
  f261: plane 99.06x99.06mm, normal (0,0,1), area 9812.9mm2, adj f208,f209,f210,f252
  f262: plane 99.06x99.06mm, normal (0,0,1), area 9812.9mm2, adj f205,f206,f207,f251
  f263: plane 99.06x99.06mm, normal (0,0,1), area 9812.9mm2, adj f202,f203,f204,f250
  f264: plane 99.06x99.06mm, normal (0,0,1), area 9812.9mm2, adj f199,f200,f201,f249
  f265: plane 99.06x99.06mm, normal (0,0,1), area 9812.9mm2, adj f196,f197,f198,f248
  f266: plane 99.06x99.06mm, normal (0,0,1), area 9812.9mm2, adj f193,f194,f195,f247
  f267: plane 99.06x99.06mm, normal (0,0,1), area 9812.9mm2, adj f190,f191,f192,f246
  f268: plane 99.06x99.06mm, normal (0,0,1), area 9812.9mm2, adj f187,f188,f189,f245
  f269: plane 99.06x99.06mm, normal (0,0,1), area 9812.9mm2, adj f184,f185,f186,f244
  f270: plane 99.06x99.06mm, normal (0,0,1), area 9812.9mm2, adj f181,f182,f183,f243
  f271: plane 99.06x99.06mm, normal (0,0,1), area 9812.9mm2, adj f178,f179,f180,f242
  f272: plane 99.06x99.06mm, normal (0,0,1), area 9812.9mm2, adj f175,f176,f177,f241
  f273: plane 99.06x99.06mm, normal (0,0,1), area 9812.9mm2, adj f172,f173,f174,f240
  f274: plane 99.06x99.06mm, normal (0,0,1), area 9812.9mm2, adj f169,f170,f171,f239
  f275: plane 99.06x99.06mm, normal (0,0,1), area 9812.9mm2, adj f166,f167,f168,f238
  f276: plane 99.06x99.06mm, normal (0,0,1), area 9812.9mm2, adj f163,f164,f165,f237
  f277: plane 99.06x99.06mm, normal (0,0,1), area 9812.9mm2, adj f160,f161,f162,f236
  f278: plane 99.06x99.06mm, normal (0,0,1), area 9812.9mm2, adj f157,f158,f159,f235
  f279: plane 99.06x99.06mm, normal (0,0,1), area 9812.9mm2, adj f154,f155,f156,f234
  f280: plane 99.06x99.06mm, normal (0,0,1), area 9812.9mm2, adj f151,f152,f153,f233
  f281: plane 99.06x99.06mm, normal (0,0,1), area 9812.9mm2, adj f148,f149,f150,f232
  f282: plane 99.06x99.06mm, normal (0,0,1), area 9812.9mm2, adj f145,f146,f147,f231
  f283: plane 99.06x99.06mm, normal (0,0,1), area 9812.9mm2, adj f142,f143,f144,f230
  f284: plane 99.06x99.06mm, normal (0,0,1), area 9812.9mm2, adj f139,f140,f141,f229
  f285: plane 99.06x99.06mm, normal (0,0,1), area 9812.9mm2, adj f136,f137,f138,f228
  f286: plane 99.06x99.06mm, normal (0,0,1), area 9812.9mm2, adj f133,f134,f135,f227
  f287: plane 99.06x99.06mm, normal (0,0,1), area 9812.9mm2, adj f130,f131,f132,f226
  f288: plane 99.06x99.06mm, normal (0,0,1), area 9812.9mm2, adj f127,f128,f129,f225
  f289: plane 99.06x99.06mm, normal (0,0,1), area 9812.9mm2, adj f124,f125,f126,f224
  f290: plane 99.06x99.06mm, normal (0,0,1), area 9812.9mm2, adj f121,f122,f123,f223
  f291: plane 99.06x99.06mm, normal (0,0,1), area 9812.9mm2, adj f118,f119,f120,f222
  f292: plane 99.06x99.06mm, normal (0,0,1), area 9812.9mm2, adj f115,f116,f117,f221
  f293: plane 99.06x99.06mm, normal (0,0,1), area 9812.9mm2, adj f112,f113,f114,f220
PLACE A t=(-50.93,-357.21,10.33)mm
PLACE B t=(1.14,-0.34,-14.2)mm
MATE fastened A.f0 <-> B.f4  axis (0,0,-1) through (-50.93,-357.21,11.2)mm
